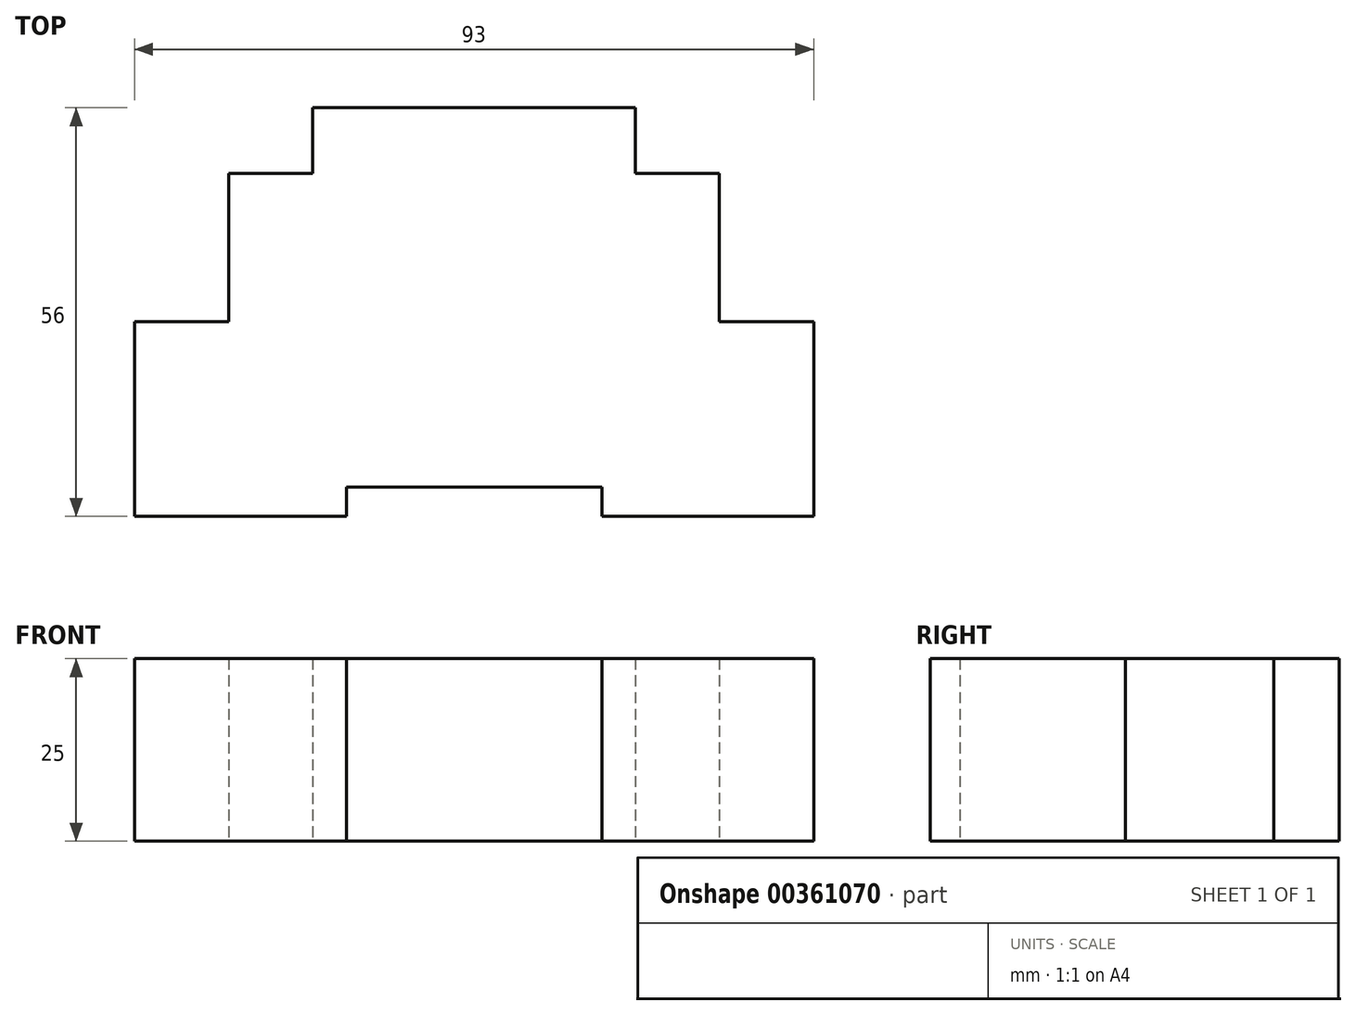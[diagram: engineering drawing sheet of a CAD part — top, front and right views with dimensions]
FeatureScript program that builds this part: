
annotation { "Feature Type Name" : "Feature", "Feature Type Description" : "" }
export const myFeature = defineFeature(function(context is Context, id is Id, definition is map)
    precondition{}
    {
        {
            var Q0;
            Q0=qCreatedBy(makeId("Top.planeOp"),FACE);
            var sketch = newSketch(context, id + "F0", { "sketchPlane" : qUnion([Q0])});
            skLineSegment(sketch, "E0", {"start": v(-64, -24.3) * mm, "end": v(-35, -24.3) * mm});
            skLineSegment(sketch, "E1", {"start": v(0, -24.3) * mm, "end": v(29, -24.3) * mm});
            skLineSegment(sketch, "E2", {"start": v(-64, -24.3) * mm, "end": v(-64, 2.4) * mm});
            skLineSegment(sketch, "E3", {"start": v(29, -24.3) * mm, "end": v(29, 2.4) * mm});
            skLineSegment(sketch, "E4", {"start": v(-64, 2.4) * mm, "end": v(-51.1, 2.4) * mm});
            skLineSegment(sketch, "E5", {"start": v(-51.1, 2.4) * mm, "end": v(-51.1, 22.7) * mm});
            skLineSegment(sketch, "E6", {"start": v(-39.6, 22.7) * mm, "end": v(-39.6, 31.7) * mm});
            skLineSegment(sketch, "E7", {"start": v(-39.6, 31.7) * mm, "end": v(4.6, 31.7) * mm});
            skLineSegment(sketch, "E8", {"start": v(4.6, 31.7) * mm, "end": v(4.6, 22.7) * mm});
            skLineSegment(sketch, "E9", {"start": v(4.6, 22.7) * mm, "end": v(16.1, 22.7) * mm});
            skLineSegment(sketch, "E10", {"start": v(16.1, 22.7) * mm, "end": v(16.1, 2.4) * mm});
            skLineSegment(sketch, "E11", {"start": v(16.1, 2.4) * mm, "end": v(29, 2.4) * mm});
            skLineSegment(sketch, "E12", {"start": v(-51.1, 22.7) * mm, "end": v(-39.6, 22.7) * mm});
            skLineSegment(sketch, "E13", {"start": v(-17.5, -20.3) * mm, "end": v(-17.5, 31.7) * mm});
            skPoint(sketch, "E14", {"position": v(-35, -24.3) * mm});
            skPoint(sketch, "E15", {"position": v(0, -24.3) * mm});
            skLineSegment(sketch, "E16", {"start": v(-35, -24.3) * mm, "end": v(-35, -20.3) * mm});
            skLineSegment(sketch, "E17", {"start": v(-35, -20.3) * mm, "end": v(0, -20.3) * mm});
            skLineSegment(sketch, "E18", {"start": v(0, -20.3) * mm, "end": v(0, -24.3) * mm});
            skPoint(sketch, "E19", {"position": v(-17.5, -20.3) * mm});
            skLineSegment(sketch, "E20", {"start": v(-35, -20.3) * mm, "end": v(-17.5, -20.3) * mm});
            skLineSegment(sketch, "E21", {"start": v(-17.5, -20.3) * mm, "end": v(0, -20.3) * mm});
            skPoint(sketch, "E22.end.orphan", {"position": v(-17.5, 22.7) * mm});
            skSolve(sketch);
        }
        {
            var Q0;
            Q0=makeQuery(id+"F0.imprint","IMPRINT",FACE,{"disambiguationData":[TD([[makeQuery(id+"F0.imprint","IMPRINT",EDGE,{"derivedFrom":sQuery(id+"F0.wireOp",EDGE,"E2")}),-1.0]])]});
            var Q1;
            Q1=makeQuery(id+"F0.imprint","IMPRINT",FACE,{"disambiguationData":[TD([[makeQuery(id+"F0.imprint","IMPRINT",EDGE,{"derivedFrom":sQuery(id+"F0.wireOp",EDGE,"E1")}),1.0]])]});
            extrude(context, id + "F1", {"entities" : qUnion([Q0, Q1]), "endBound" : BoundingType.SYMMETRIC, "depth" : 25 * mm});
        }
    });
